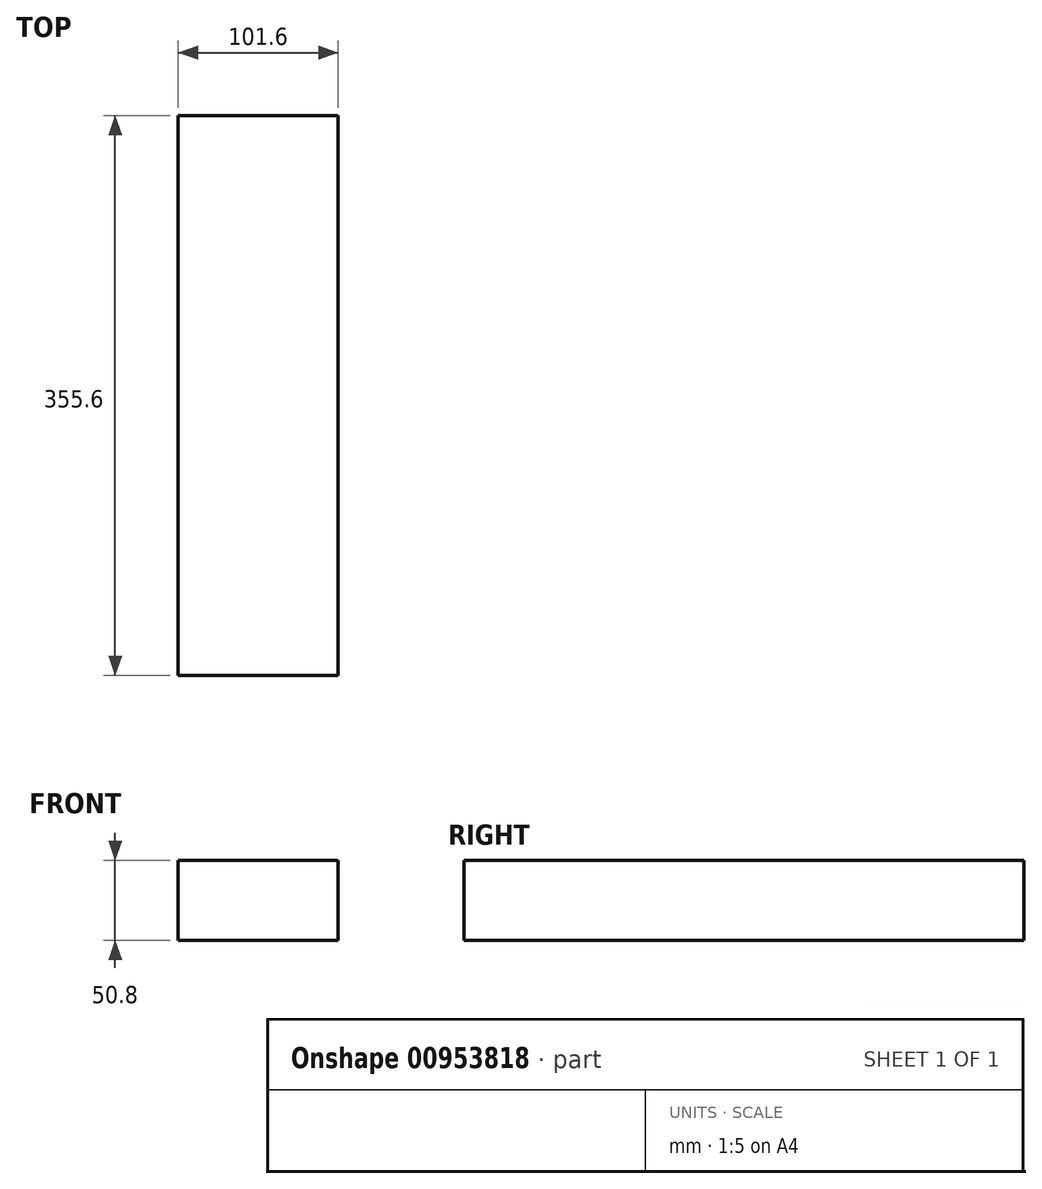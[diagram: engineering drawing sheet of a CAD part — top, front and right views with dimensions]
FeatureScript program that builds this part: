
annotation { "Feature Type Name" : "Feature", "Feature Type Description" : "" }
export const myFeature = defineFeature(function(context is Context, id is Id, definition is map)
    precondition{}
    {
        {
            var Q0;
            Q0=qCreatedBy(makeId("Front.planeOp"),FACE);
            var sketch = newSketch(context, id + "F0", { "sketchPlane" : qUnion([Q0])});
            skLineSegment(sketch, "E0.bottom", {"start": v(-50.8, -25.4) * mm, "end": v(50.8, -25.4) * mm});
            skLineSegment(sketch, "E0.top", {"start": v(-50.8, 25.4) * mm, "end": v(50.8, 25.4) * mm});
            skLineSegment(sketch, "E0.left", {"start": v(-50.8, -25.4) * mm, "end": v(-50.8, 25.4) * mm});
            skLineSegment(sketch, "E0.right", {"start": v(50.8, -25.4) * mm, "end": v(50.8, 25.4) * mm});
            skPoint(sketch, "E0.middle", {"position": v(0, 0) * mm});
            skSolve(sketch);
        }
        {
            var Q0;
            Q0 = qSketchRegion(id + "F0", true);
            extrude(context, id + "F1", {"entities" : qUnion([Q0]), "depth" : 355.6 * mm, "offsetDistance" : 25.4 * mm});
        }
    });
